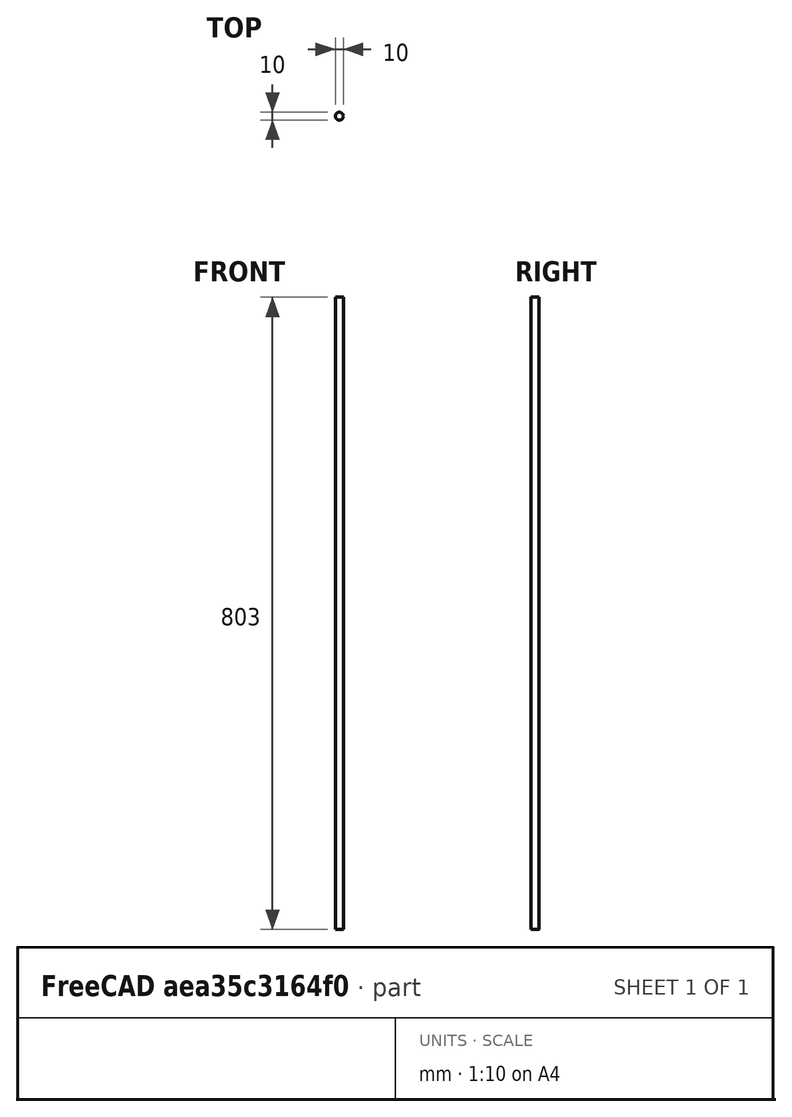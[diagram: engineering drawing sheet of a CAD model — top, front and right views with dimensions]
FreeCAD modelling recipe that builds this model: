
FCSTD DOCUMENT  (FreeCAD 0.14R3702 (Git))
Label: rm1605_800mm
License: CC-BY 3.0
LicenseURL: http://creativecommons.org/licenses/by/3.0/
objects: Part::Feature×3, Sketcher::SketchObject×1, PartDesign::Pad×1
note: 6 computed .brp shape members not serialized (recipe doc carries the construction recipe); baked Part::Feature solids carry a one-line shape summary decoded from their .brp

FEATURE [Sketcher::SketchObject] Sketch
  sketch-geometry (1):
    g0: Circle CenterX=0 CenterY=0 CenterZ=0 NormalX=0 NormalY=0 NormalZ=1 Radius=5
  constraints (2):
    c: Coincident(g0,g-1)
    c: Radius(g0) = 5
FEATURE [PartDesign::Pad] Pad
  Length = 803
  Length2 = 33.15
  Sketch = -> Sketch
  Type = 0
FEATURE [Part::Feature] Face
  shape: bbox 15.55 x 14.23 x 2e-07 mm, 1 faces, 0 solids (baked)
FEATURE [Part::Feature] Face001
  shape: bbox 19.81 x 19.02 x 2.002e-07 mm, 1 faces, 0 solids (baked)
FEATURE [Part::Feature] Cut001_solid  label="Cut001 (Solid)"
  shape: bbox 21.72 x 24.36 x 749.5 mm, 446 faces (baked)
